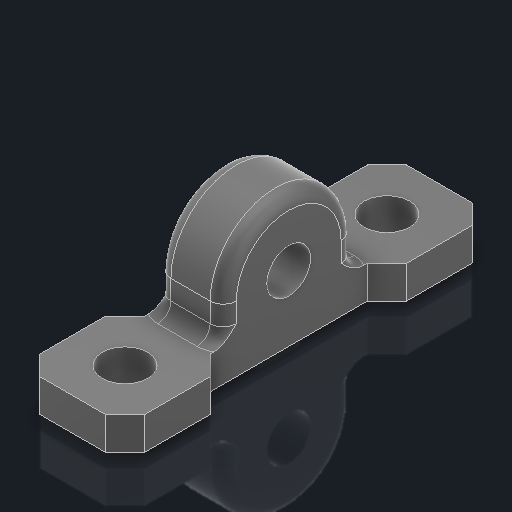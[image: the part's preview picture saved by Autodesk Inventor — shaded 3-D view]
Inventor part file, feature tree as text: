
AUTODESK INVENTOR PART (.ipt)
format: ipt  version: 2023.2 (Build 272271030, 271C)  size: 262,656 bytes
history: native  units: in
note: dims shown in document units (in); Inventor stores cm internally (conversion verified against a paired STEP export)
features: extrude x3, sketch x3, fillet x1
ambient origin geometry x8: Origin, YZ Plane, XZ Plane, XY Plane, X Axis, Y Axis, Z Axis, Center Point
bodies: Solid1 (feature_tree)
feature tree (7):
  extrude  "Extrusion1"  Depth=0.173in
  extrude  "Extrusion2"  Depth=0.4in
  extrude  "Extrusion3"  Depth=0.05in
  fillet  "Fillet1"  Radius=0.4in
  sketch  "Sketch1"  dims[d2=0.173in d3=0.173in]
  sketch  "Sketch2"  dims[d4=1.0in d8=0.4in]
  sketch  "Sketch3"  dims[d9=0.4in d10=0.4in d11=0.4in d12=0.6in d13=0.2in d14=0.2in d15=0.2in d16=0.25in d17=0.075in d18=0.075in d19=0.075in d20=0.075in d21=0.075in d22=0.075in d23=0.075in d24=0.075in d25=0.075in d26=0.075in d27=0.075in d28=0.075in d29=0.075in d30=0.075in d31=0.075in d32=0.075in d33=0.075in d34=0.125in d35=0.0in d36=0.176in d37=0.176in d38=0.037in d39=0.612in d40=0.02in d41=0.027in d42=0.0in d43=0.167in d44=0.25in d45=0.3in d46=0.5in d47=0.5in d48=0.25in d49=0.25in d50=0.027in d51=0.0in d52=0.05in]
